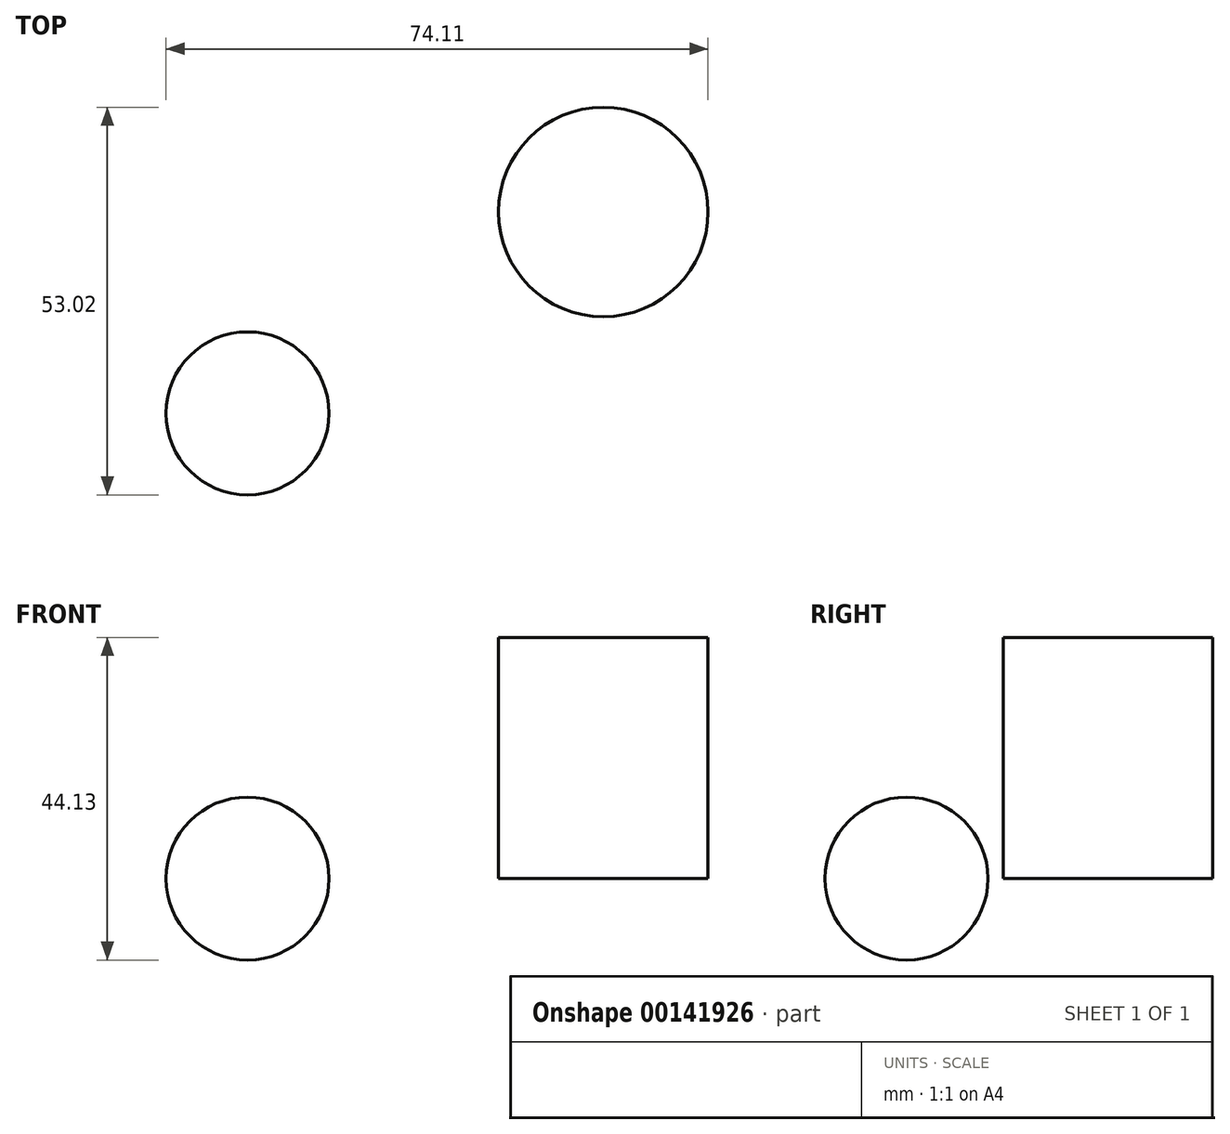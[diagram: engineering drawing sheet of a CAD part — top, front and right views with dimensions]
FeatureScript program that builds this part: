
annotation { "Feature Type Name" : "Feature", "Feature Type Description" : "" }
export const myFeature = defineFeature(function(context is Context, id is Id, definition is map)
    precondition{}
    {
        {
            var Q0;
            Q0=qCreatedBy(makeId("Front.planeOp"),FACE);
            var sketch = newSketch(context, id + "F0", { "sketchPlane" : qUnion([Q0])});
            skLineSegment(sketch, "E0", {"start": v(0, 33) * mm, "end": v(0, 0) * mm});
            skLineSegment(sketch, "E1.bottom", {"start": v(0, 33) * mm, "end": v(-14.33, 33) * mm});
            skLineSegment(sketch, "E1.top", {"start": v(0, 0) * mm, "end": v(-14.33, 0) * mm});
            skLineSegment(sketch, "E1.right", {"start": v(-14.33, 33) * mm, "end": v(-14.33, 0) * mm});
            skSolve(sketch);
        }
        {
            var Q0;
            Q0=makeQuery(id+"F0.imprint","IMPRINT",FACE,{"disambiguationData":[TD([[makeQuery(id+"F0.imprint","IMPRINT",EDGE,{"derivedFrom":sQuery(id+"F0.wireOp",EDGE,"E1.bottom")}),1.0]])]});
            var Q1;
            Q1=sQuery(id+"F0.wireOp",EDGE,"E0");
            revolve(context, id + "F1", {"entities" : qUnion([Q0]), "axis" : qUnion([Q1]), "revolveType" : RevolveType.FULL});
        }
        {
            var Q0;
            Q0=qCreatedBy(makeId("Top.planeOp"),FACE);
            var sketch = newSketch(context, id + "F2", { "sketchPlane" : qUnion([Q0])});
            skCircle(sketch, "E2", {"center": v(-48.63, -27.54) * mm, "radius": 11.14 * mm});
            skLineSegment(sketch, "E3", {"start": v(-48.63, -27.54) * mm, "end": v(-48.63, -38.69) * mm});
            skLineSegment(sketch, "E4", {"start": v(-48.63, -38.69) * mm, "end": v(-48.63, -16.4) * mm});
            skCircle(sketch, "E5", {"center": v(47.82, 0) * mm, "radius": 12.18 * mm});
            skSolve(sketch);
        }
        {
            var Q0;
            {var subQ0=sQuery(id+"F2.wireOp",EDGE,"E4");var subQ4=makeQuery(id+"F2.imprint","IMPRINT",VERTEX,{"derivedFrom":subQ0});Q0=makeQuery(id+"F2.imprint","IMPRINT",FACE,{"disambiguationData":[TD([[makeQuery(id+"F2.imprint","IMPRINT",EDGE,{"disambiguationData":[TD([[subQ4,1.0]])],"derivedFrom":subQ0}),1.0]])]});}
            var Q1;
            Q1=sQuery(id+"F2.wireOp",EDGE,"E4");
            revolve(context, id + "F3", {"entities" : qUnion([Q0]), "axis" : qUnion([Q1]), "revolveType" : RevolveType.FULL});
        }
        {
            var Q0;
            Q0=qCreatedBy(makeId("Front.planeOp"),FACE);
            var sketch = newSketch(context, id + "F4", { "sketchPlane" : qUnion([Q0])});
            skLineSegment(sketch, "E6", {"start": v(0, 0) * mm, "end": v(0, -30.39) * mm});
            skLineSegment(sketch, "E7", {"start": v(-14.39, 0) * mm, "end": v(0, -30.39) * mm});
            skLineSegment(sketch, "E8", {"start": v(0, -30.39) * mm, "end": v(-13.56, 0) * mm});
            skSolve(sketch);
        }
        {
            var Q0;
            Q0=sQuery(id+"F4.wireOp",EDGE,"E8");
            var Q1;
            Q1=sQuery(id+"F4.wireOp",EDGE,"E6");
            revolve(context, id + "F5", {"bodyType" : ToolBodyType.SURFACE, "surfaceEntities" : qUnion([Q0]), "axis" : qUnion([Q1]), "revolveType" : RevolveType.FULL});
        }
    });
